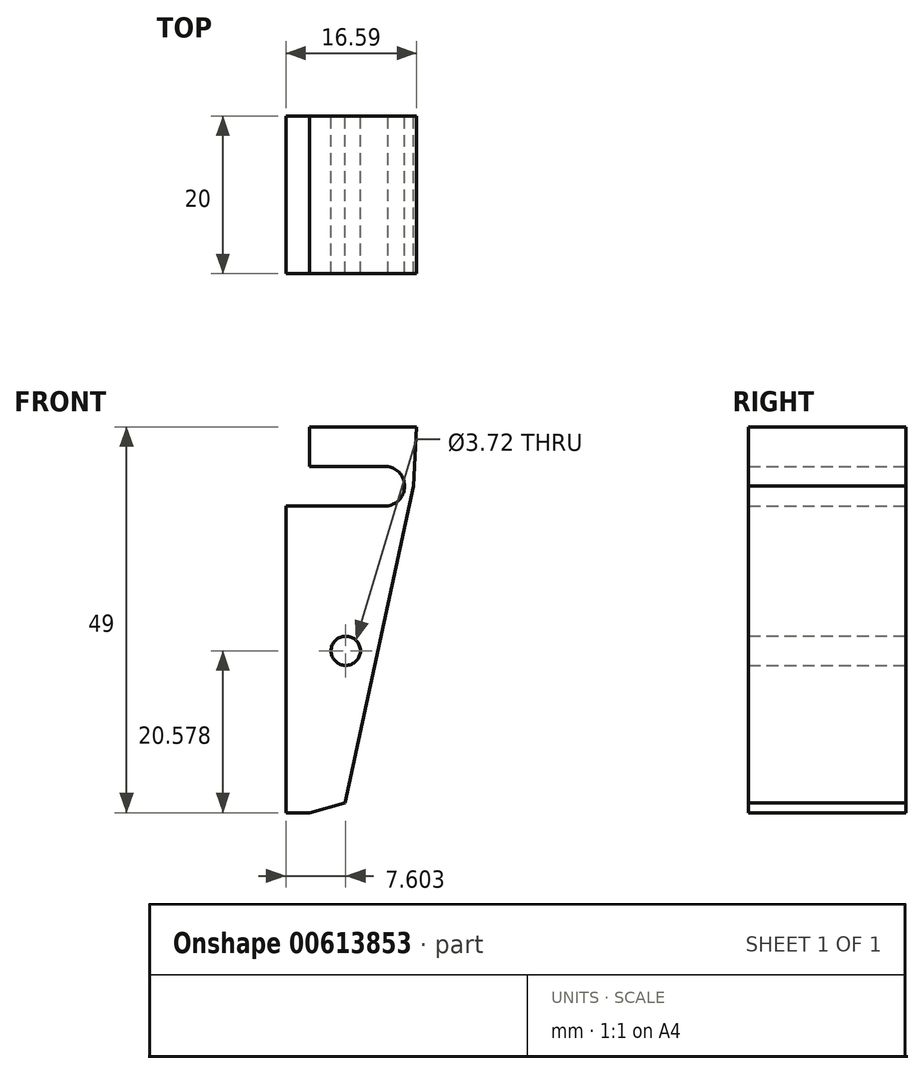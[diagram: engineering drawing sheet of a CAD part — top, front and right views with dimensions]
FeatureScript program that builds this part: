
annotation { "Feature Type Name" : "Feature", "Feature Type Description" : "" }
export const myFeature = defineFeature(function(context is Context, id is Id, definition is map)
    precondition{}
    {
        {
            var Q0;
            Q0=qCreatedBy(makeId("Front.planeOp"),FACE);
            var sketch = newSketch(context, id + "F0", { "sketchPlane" : qUnion([Q0])});
            skLineSegment(sketch, "E0.MirrorCS", {"start": v(15.77, 17.85) * mm, "end": v(16.16, 25.35) * mm});
            skLineSegment(sketch, "E1.MirrorCS", {"start": v(7.1, -22.4) * mm, "end": v(15.77, 17.85) * mm});
            skLineSegment(sketch, "E2.MirrorCS", {"start": v(2.57, -23.65) * mm, "end": v(7.1, -22.4) * mm});
            skLineSegment(sketch, "E3.MirrorCS", {"start": v(2.57, 20.35) * mm, "end": v(2.57, 25.35) * mm});
            skLineSegment(sketch, "E4.MirrorCS", {"start": v(12.57, 20.35) * mm, "end": v(2.57, 20.35) * mm});
            skArc(sketch, "E5.MirrorCS", {"start": v(12.57, 20.35) * mm, "mid": v(14.64, 17.85) * mm, "end": v(12.57, 15.35) * mm});
            skLineSegment(sketch, "E6.MirrorCS", {"start": v(2.57, 15.35) * mm, "end": v(12.57, 15.35) * mm});
            skLineSegment(sketch, "E7.MirrorCS", {"start": v(2.57, -23.65) * mm, "end": v(2.57, 11.35) * mm});
            skLineSegment(sketch, "E8", {"start": v(2.57, 25.35) * mm, "end": v(16.16, 25.35) * mm});
            skLineSegment(sketch, "E9.MirrorCS", {"start": v(-2.43, -23.65) * mm, "end": v(-2.43, 11.35) * mm});
            skLineSegment(sketch, "E10.MirrorCS", {"start": v(-2.43, 15.35) * mm, "end": v(-12.43, 15.35) * mm});
            skArc(sketch, "E11.MirrorCS", {"start": v(-12.43, 20.35) * mm, "mid": v(-14.5, 17.85) * mm, "end": v(-12.43, 15.35) * mm});
            skLineSegment(sketch, "E12.MirrorCS", {"start": v(-12.43, 20.35) * mm, "end": v(-2.43, 20.35) * mm});
            skLineSegment(sketch, "E13.MirrorCS", {"start": v(-2.43, 20.35) * mm, "end": v(-2.43, 25.35) * mm});
            skLineSegment(sketch, "E14.MirrorCS", {"start": v(-2.43, 25.35) * mm, "end": v(-16.01, 25.35) * mm});
            skLineSegment(sketch, "E15.MirrorCS", {"start": v(-15.62, 17.85) * mm, "end": v(-16.01, 25.35) * mm});
            skLineSegment(sketch, "E16.MirrorCS", {"start": v(-6.96, -22.4) * mm, "end": v(-15.62, 17.85) * mm});
            skLineSegment(sketch, "E17.MirrorCS", {"start": v(-2.43, -23.65) * mm, "end": v(-6.96, -22.4) * mm});
            skLineSegment(sketch, "E18", {"start": v(-11.94, 17.85) * mm, "end": v(12.1, 17.85) * mm, "construction": true});
            skLineSegment(sketch, "E19", {"start": v(51.96, 17.85) * mm, "end": v(12.1, 17.85) * mm, "construction": true});
            skLineSegment(sketch, "E20", {"start": v(-11.94, 17.85) * mm, "end": v(-36.5, 17.85) * mm, "construction": true});
            skLineSegment(sketch, "E21", {"start": v(-2.43, 20.35) * mm, "end": v(-2.43, 15.35) * mm, "construction": true});
            skLineSegment(sketch, "E22", {"start": v(-2.43, 15.35) * mm, "end": v(-2.43, 11.35) * mm});
            skLineSegment(sketch, "E23", {"start": v(2.57, 15.35) * mm, "end": v(2.57, 11.35) * mm});
            skLineSegment(sketch, "E24", {"start": v(-11.55, 15.3) * mm, "end": v(-7.34, -4.26) * mm, "construction": true});
            skCircle(sketch, "E25", {"center": v(-7.57, -3.19) * mm, "radius": 1.86 * mm});
            skCircle(sketch, "E26.MirrorC", {"center": v(7.17, -3.07) * mm, "radius": 1.86 * mm});
            skLineSegment(sketch, "E27", {"start": v(2.57, 15.35) * mm, "end": v(-0.43, 15.35) * mm});
            skLineSegment(sketch, "E28", {"start": v(-0.43, 15.35) * mm, "end": v(-0.43, -23.65) * mm});
            skLineSegment(sketch, "E29", {"start": v(-0.43, -23.65) * mm, "end": v(2.57, -23.65) * mm});
            skSolve(sketch);
        }
        {
            var Q0;
            Q0=makeQuery(id+"F0.imprint","IMPRINT",FACE,{"disambiguationData":[TD([[makeQuery(id+"F0.imprint","IMPRINT",EDGE,{"derivedFrom":sQuery(id+"F0.wireOp",EDGE,"E0.MirrorCS")}),1.0]])]});
            var Q1;
            Q1=makeQuery(id+"F0.imprint","IMPRINT",FACE,{"disambiguationData":[TD([[makeQuery(id+"F0.imprint","IMPRINT",EDGE,{"derivedFrom":sQuery(id+"F0.wireOp",EDGE,"E7.MirrorCS")}),1.0]])]});
            extrude(context, id + "F1", {"entities" : qUnion([Q0, Q1]), "depth" : 20 * mm, "offsetDistance" : 25 * mm});
        }
    });
